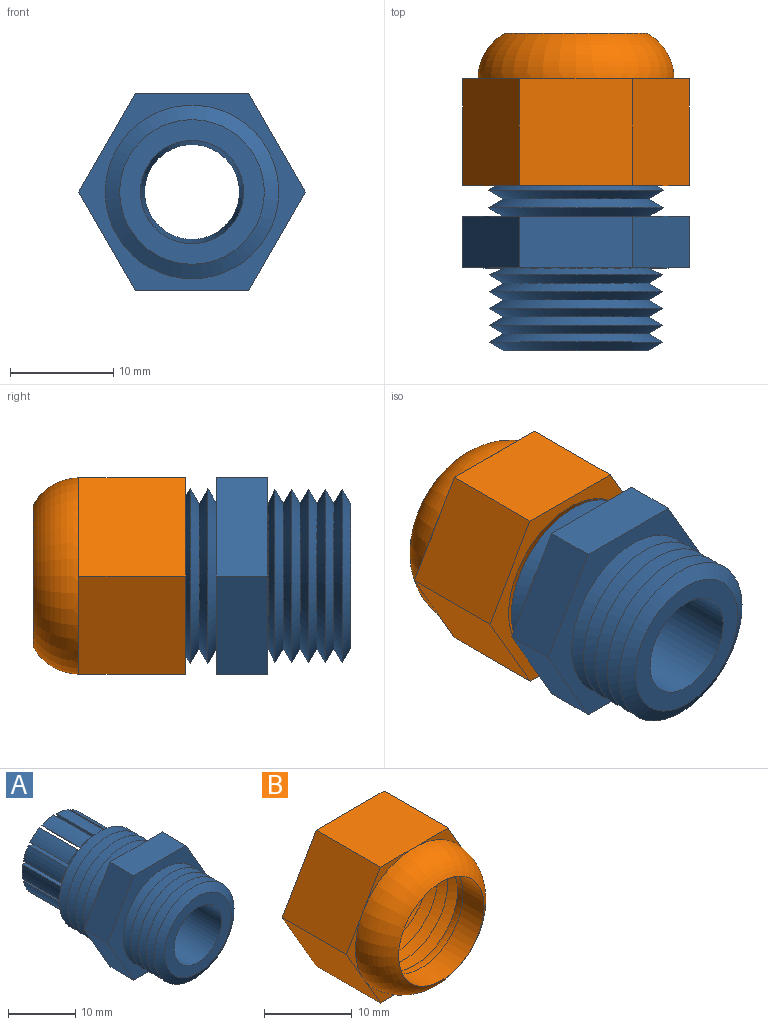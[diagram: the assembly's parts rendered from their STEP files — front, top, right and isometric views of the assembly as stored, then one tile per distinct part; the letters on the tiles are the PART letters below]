
ASSEMBLY  parts=2 mates=1
PART A: 119 faces, bbox 21.9x30x19 mm
  f0: cone r=5.75mm half-angle=2.7deg, axis (0,-1,0), area 15.8mm2, adj f1,f64,f116,f117
  f1: plane 2.55x2.24mm, normal (0,1,0), area 3.7mm2, adj f0,f2,f116,f117
  f2: cylinder r=7mm len=8mm, axis (0,-1,0), area 21mm2, adj f1,f3,f116,f117
  f3: plane 2.55x1mm, normal (0,-1,0), area 1.1mm2, adj f2,f69,f116,f117
  f4: cone r=5.75mm half-angle=2.7deg, axis (0,-1,0), area 15.8mm2, adj f5,f64,f114,f115
  f5: plane 3x1.89mm, normal (0,1,0), area 3.7mm2, adj f4,f6,f114,f115
  f6: cylinder r=7mm len=8mm, axis (0,-1,0), area 21mm2, adj f5,f7,f114,f115
  f7: plane 2.66x0.92mm, normal (0,-1,0), area 1.1mm2, adj f6,f69,f114,f115
  f8: cone r=5.75mm half-angle=2.7deg, axis (0,-1,0), area 15.8mm2, adj f9,f64,f112,f113
  f9: plane 3.16x2.31mm, normal (0,1,0), area 3.7mm2, adj f8,f10,f112,f113
  f10: cylinder r=7mm len=8mm, axis (0,-1,0), area 21mm2, adj f9,f11,f112,f113
  f11: plane 2.33x1.81mm, normal (0,-1,0), area 1.1mm2, adj f10,f69,f112,f113
  f12: cone r=5.75mm half-angle=2.7deg, axis (0,-1,0), area 15.8mm2, adj f13,f64,f110,f111
  f13: plane 2.68x2.36mm, normal (0,1,0), area 3.7mm2, adj f12,f14,f110,f111
  f14: cylinder r=7mm len=8mm, axis (0,-1,0), area 21mm2, adj f13,f15,f110,f111
  f15: plane 2.36x1.53mm, normal (0,-1,0), area 1.1mm2, adj f14,f69,f110,f111
  f16: cone r=5.75mm half-angle=2.7deg, axis (0,-1,0), area 15.8mm2, adj f17,f64,f108,f109
  f17: plane 2.7x1.81mm, normal (0,1,0), area 3.7mm2, adj f16,f18,f108,f109
  f18: cylinder r=7mm len=8mm, axis (0,-1,0), area 21mm2, adj f17,f19,f108,f109
  f19: plane 2.63x0.55mm, normal (0,-1,0), area 1.1mm2, adj f18,f69,f108,f109
  f20: cone r=5.75mm half-angle=2.7deg, axis (0,-1,0), area 15.8mm2, adj f21,f64,f106,f107
  f21: plane 3.16x2.15mm, normal (0,1,0), area 3.7mm2, adj f20,f22,f106,f107
  f22: cylinder r=7mm len=8mm, axis (0,-1,0), area 21mm2, adj f21,f23,f106,f107
  f23: plane 2.56x1.4mm, normal (0,-1,0), area 1.1mm2, adj f22,f69,f106,f107
  f24: cone r=5.75mm half-angle=2.7deg, axis (0,-1,0), area 15.8mm2, adj f25,f64,f104,f105
  f25: plane 3x2.34mm, normal (0,1,0), area 3.7mm2, adj f24,f26,f104,f105
  f26: cylinder r=7mm len=8mm, axis (0,-1,0), area 21mm2, adj f25,f27,f104,f105
  f27: plane 2.12x1.98mm, normal (0,-1,0), area 1.1mm2, adj f26,f69,f104,f105
  f28: cone r=5.75mm half-angle=2.7deg, axis (0,-1,0), area 15.8mm2, adj f29,f64,f102,f103
  f29: plane 2.55x2.24mm, normal (0,1,0), area 3.7mm2, adj f28,f30,f102,f103
  f30: cylinder r=7mm len=8mm, axis (0,-1,0), area 21mm2, adj f29,f31,f102,f103
  f31: plane 2.55x1mm, normal (0,-1,0), area 1.1mm2, adj f30,f69,f102,f103
  f32: cone r=5.75mm half-angle=2.7deg, axis (0,-1,0), area 15.8mm2, adj f33,f64,f100,f101
  f33: plane 3x1.89mm, normal (0,1,0), area 3.7mm2, adj f32,f34,f100,f101
  f34: cylinder r=7mm len=8mm, axis (0,-1,0), area 21mm2, adj f33,f35,f100,f101
  f35: plane 2.66x0.92mm, normal (0,-1,0), area 1.1mm2, adj f34,f69,f100,f101
  f36: cone r=5.75mm half-angle=2.7deg, axis (0,-1,0), area 15.8mm2, adj f37,f64,f98,f99
  f37: plane 3.16x2.31mm, normal (0,1,0), area 3.7mm2, adj f36,f38,f98,f99
  f38: cylinder r=7mm len=8mm, axis (0,-1,0), area 21mm2, adj f37,f39,f98,f99
  f39: plane 2.33x1.81mm, normal (0,-1,0), area 1.1mm2, adj f38,f69,f98,f99
  f40: cone r=5.75mm half-angle=2.7deg, axis (0,-1,0), area 15.8mm2, adj f41,f64,f96,f97
  f41: plane 2.68x2.36mm, normal (0,1,0), area 3.7mm2, adj f40,f42,f96,f97
  f42: cylinder r=7mm len=8mm, axis (0,-1,0), area 21mm2, adj f41,f43,f96,f97
  f43: plane 2.36x1.53mm, normal (0,-1,0), area 1.1mm2, adj f42,f69,f96,f97
  f44: cone r=5.75mm half-angle=2.7deg, axis (0,-1,0), area 15.8mm2, adj f45,f64,f94,f95
  f45: plane 2.7x1.81mm, normal (0,1,0), area 3.7mm2, adj f44,f46,f94,f95
  f46: cylinder r=7mm len=8mm, axis (0,-1,0), area 21mm2, adj f45,f47,f94,f95
  f47: plane 2.63x0.55mm, normal (0,-1,0), area 1.1mm2, adj f46,f69,f94,f95
  f48: cone r=5.75mm half-angle=2.7deg, axis (0,-1,0), area 15.8mm2, adj f49,f64,f92,f93
  f49: plane 3.16x2.15mm, normal (0,1,0), area 3.7mm2, adj f48,f50,f92,f93
  f50: cylinder r=7mm len=8mm, axis (0,-1,0), area 21mm2, adj f49,f51,f92,f93
  f51: plane 2.56x1.4mm, normal (0,-1,0), area 1.1mm2, adj f50,f69,f92,f93
  f52: cone r=8.48mm half-angle=60deg, axis (0,1,0), area 80.3mm2, adj f62,f71
  f53: plane 14x14mm, normal (0,1,0), area 18mm2, adj f54,f69
  f54: cone r=7mm half-angle=60deg, axis (0,-1,0), area 83.2mm2, adj f53,f55
  f55: cone r=8.48mm half-angle=60deg, axis (0,1,0), area 83.2mm2, adj f54,f56
  f56: cone r=7mm half-angle=60deg, axis (0,-1,0), area 83.2mm2, adj f55,f57
  f57: cone r=8.48mm half-angle=60deg, axis (0,1,0), area 83.2mm2, adj f56,f58
  f58: cone r=7mm half-angle=60deg, axis (0,-1,0), area 83.2mm2, adj f57,f59
  f59: cone r=8.48mm half-angle=60deg, axis (0,1,0), area 83.2mm2, adj f58,f60
  f60: cone r=7mm half-angle=60deg, axis (0,-1,0), area 83.2mm2, adj f59,f61
  f61: cone r=8.48mm half-angle=60deg, axis (0,1,0), area 83.2mm2, adj f60,f62
  f62: cone r=7mm half-angle=60deg, axis (0,-1,0), area 83.2mm2, adj f52,f61
  f63: cone r=5mm half-angle=2.7deg, axis (0,-1,0), area 262.5mm2, adj f64,f90
  f64: plane 13.15x12.97mm, normal (0,1,0), area 43.7mm2, adj f0,f4,f8,f12,f16,f20,f24,f28
  f65: cone r=5.75mm half-angle=2.7deg, axis (0,-1,0), area 15.8mm2, adj f64,f66,f91,f118
  f66: plane 3x2.34mm, normal (0,1,0), area 3.7mm2, adj f65,f67,f91,f118
  f67: cylinder r=7mm len=8mm, axis (0,-1,0), area 21mm2, adj f66,f68,f91,f118
  f68: plane 2.12x1.98mm, normal (0,-1,0), area 1.1mm2, adj f67,f69,f91,f118
  f69: cylinder r=6.58mm len=13.15mm, axis (0,-1,0), area 18.4mm2, adj f3,f7,f11,f15,f19,f23,f27,f31
  f70: plane 21.94x19mm, normal (0,-1,0), area 158.7mm2, adj f72,f73,f74,f75,f76,f77,f83
  f71: plane 21.94x19mm, normal (0,1,0), area 156.1mm2, adj f52,f72,f73,f74,f75,f76,f77
  f72: plane 9.5x5.49mm, normal (0.87,0,-0.5), area 54.8mm2, adj f70,f71,f73,f77
  f73: plane 9.5x5.49mm, normal (0.87,0,0.5), area 54.8mm2, adj f70,f71,f72,f74
  f74: plane 10.97x5mm, normal (0,0,1), area 54.8mm2, adj f70,f71,f73,f75
  f75: plane 9.5x5.49mm, normal (-0.87,0,0.5), area 54.8mm2, adj f70,f71,f74,f76
  f76: plane 9.5x5.49mm, normal (-0.87,0,-0.5), area 54.8mm2, adj f70,f71,f75,f77
  f77: plane 10.97x5mm, normal (0,0,-1), area 54.8mm2, adj f70,f71,f72,f76
  f78: cone r=7mm half-angle=60deg, axis (0,-1,0), area 78.8mm2, adj f79,f84
  f79: cone r=8.41mm half-angle=60deg, axis (0,1,0), area 78.8mm2, adj f78,f80
  f80: cone r=7mm half-angle=60deg, axis (0,-1,0), area 78.8mm2, adj f79,f81
  f81: cone r=8.41mm half-angle=60deg, axis (0,1,0), area 78.8mm2, adj f80,f82
  f82: cone r=7mm half-angle=65.6deg, axis (0,-1,0), area 75mm2, adj f81,f83
  f83: cylinder r=7mm len=14mm, axis (0,-1,0), area 1.5mm2, adj f70,f82
  f84: cone r=8.41mm half-angle=60deg, axis (0,1,0), area 78.8mm2, adj f78,f85
  f85: cone r=7mm half-angle=60deg, axis (0,-1,0), area 78.8mm2, adj f84,f86
  f86: cone r=8.41mm half-angle=60deg, axis (0,1,0), area 78.8mm2, adj f85,f87
  f87: cone r=7mm half-angle=60deg, axis (0,-1,0), area 78.8mm2, adj f86,f88
  f88: cone r=8.41mm half-angle=60deg, axis (0,1,0), area 78.8mm2, adj f87,f89
  f89: plane 14x14mm, normal (0,-1,0), area 75.4mm2, adj f88,f90
  f90: cylinder r=5mm len=13.27mm, axis (0,-1,0), area 416.8mm2, adj f63,f89
  f91: plane 8x1.38mm, normal (-0.81,0,0.58), area 11.9mm2, adj f64,f65,f66,f67,f68
  f92: plane 8.01x1.42mm, normal (0.81,0,-0.58), area 12.2mm2, adj f48,f49,f50,f51,f64
  f93: plane 8x1.49mm, normal (-0.48,0,0.88), area 11.9mm2, adj f48,f49,f50,f51,f64
  f94: plane 8.01x1.53mm, normal (0.48,0,-0.88), area 12.2mm2, adj f44,f45,f46,f47,f64
  f95: plane 8x1.69mm, normal (-0.05,0,1), area 11.9mm2, adj f44,f45,f46,f47,f64
  f96: plane 8.01x1.74mm, normal (0.05,0,-1), area 12.2mm2, adj f40,f41,f42,f43,f64
  f97: plane 8x1.56mm, normal (0.39,0,0.92), area 11.9mm2, adj f40,f41,f42,f43,f64
  f98: plane 8.01x1.61mm, normal (-0.39,0,-0.92), area 12.2mm2, adj f36,f37,f38,f39,f64
  f99: plane 8x1.27mm, normal (0.75,0,0.66), area 11.9mm2, adj f36,f37,f38,f39,f64
  f100: plane 8.01x1.31mm, normal (-0.75,0,-0.66), area 12.2mm2, adj f32,f33,f34,f35,f64
  f101: plane 8x1.63mm, normal (0.96,0,0.27), area 11.9mm2, adj f32,f33,f34,f35,f64
  f102: plane 8.01x1.68mm, normal (-0.96,0,-0.27), area 12.2mm2, adj f28,f29,f30,f31,f64
  f103: plane 8x1.67mm, normal (0.99,0,-0.17), area 11.9mm2, adj f28,f29,f30,f31,f64
  f104: plane 8.01x1.72mm, normal (-0.99,0,0.17), area 12.2mm2, adj f24,f25,f26,f27,f64
  f105: plane 8x1.38mm, normal (0.81,0,-0.58), area 11.9mm2, adj f24,f25,f26,f27,f64
  f106: plane 8.01x1.42mm, normal (-0.81,0,0.58), area 12.2mm2, adj f20,f21,f22,f23,f64
  f107: plane 8x1.49mm, normal (0.48,0,-0.88), area 11.9mm2, adj f20,f21,f22,f23,f64
  f108: plane 8.01x1.53mm, normal (-0.48,0,0.88), area 12.2mm2, adj f16,f17,f18,f19,f64
  f109: plane 8x1.69mm, normal (0.05,0,-1), area 11.9mm2, adj f16,f17,f18,f19,f64
  f110: plane 8.01x1.74mm, normal (-0.05,0,1), area 12.2mm2, adj f12,f13,f14,f15,f64
  f111: plane 8x1.56mm, normal (-0.39,0,-0.92), area 11.9mm2, adj f12,f13,f14,f15,f64
  f112: plane 8.01x1.61mm, normal (0.39,0,0.92), area 12.2mm2, adj f8,f9,f10,f11,f64
  f113: plane 8x1.27mm, normal (-0.75,0,-0.66), area 11.9mm2, adj f8,f9,f10,f11,f64
  f114: plane 8.01x1.31mm, normal (0.75,0,0.66), area 12.2mm2, adj f4,f5,f6,f7,f64
  f115: plane 8x1.63mm, normal (-0.96,0,-0.27), area 11.9mm2, adj f4,f5,f6,f7,f64
  f116: plane 8.01x1.68mm, normal (0.96,0,0.27), area 12.2mm2, adj f0,f1,f2,f3,f64
  f117: plane 8x1.67mm, normal (-0.99,0,0.17), area 11.9mm2, adj f0,f1,f2,f3,f64
  f118: plane 8.01x1.72mm, normal (0.99,0,-0.17), area 12.2mm2, adj f64,f65,f66,f67,f68
PART B: 29 faces, bbox 21.9x14.9x19 mm
  f0: plane 8.23x4.75mm, normal (0,-1,0), area 4.9mm2, adj f7,f8,f26
  f1: plane 9.5x2.74mm, normal (0,-1,0), area 4.9mm2, adj f6,f7,f26
  f2: plane 8.23x4.75mm, normal (0,-1,0), area 4.9mm2, adj f6,f11,f26
  f3: plane 8.23x4.75mm, normal (0,-1,0), area 4.9mm2, adj f10,f11,f26
  f4: plane 9.5x2.74mm, normal (0,-1,0), area 4.9mm2, adj f9,f10,f26
  f5: plane 8.23x4.75mm, normal (0,-1,0), area 4.9mm2, adj f8,f9,f26
  f6: plane 10.36x9.5mm, normal (0.87,0,0.5), area 113.6mm2, adj f1,f2,f7,f11,f12
  f7: plane 10.36x9.5mm, normal (0.87,0,-0.5), area 113.6mm2, adj f0,f1,f6,f8,f12
  f8: plane 10.97x10.36mm, normal (0,0,-1), area 113.6mm2, adj f0,f5,f7,f9,f12
  f9: plane 10.36x9.5mm, normal (-0.87,0,-0.5), area 113.6mm2, adj f4,f5,f8,f10,f12
  f10: plane 10.36x9.5mm, normal (-0.87,0,0.5), area 113.6mm2, adj f3,f4,f9,f11,f12
  f11: plane 10.97x10.36mm, normal (0,0,1), area 113.6mm2, adj f2,f3,f6,f10,f12
  f12: plane 21.94x19mm, normal (0,1,0), area 90.4mm2, adj f6,f7,f8,f9,f10,f11,f13
  f13: cone r=8.41mm half-angle=67.3deg, axis (0,1,0), area 74mm2, adj f12,f14
  f14: cone r=7mm half-angle=60deg, axis (0,-1,0), area 78.8mm2, adj f13,f15
  f15: cone r=8.41mm half-angle=60deg, axis (0,1,0), area 78.8mm2, adj f14,f16
  f16: cone r=7mm half-angle=60deg, axis (0,-1,0), area 78.8mm2, adj f15,f17
  f17: cone r=8.41mm half-angle=60deg, axis (0,1,0), area 78.8mm2, adj f16,f18
  f18: cone r=7mm half-angle=60deg, axis (0,-1,0), area 78.8mm2, adj f17,f19
  f19: cone r=8.41mm half-angle=60deg, axis (0,1,0), area 78.8mm2, adj f18,f20
  f20: cone r=7mm half-angle=60deg, axis (0,-1,0), area 78.8mm2, adj f19,f21
  f21: cone r=8.41mm half-angle=60deg, axis (0,1,0), area 78.8mm2, adj f20,f22
  f22: cone r=7mm half-angle=60deg, axis (0,-1,0), area 78.8mm2, adj f21,f23
  f23: cone r=8.41mm half-angle=60deg, axis (0,1,0), area 78.8mm2, adj f22,f24
  f24: cone r=7mm half-angle=60deg, axis (0,-1,0), area 78.8mm2, adj f23,f25
  f25: cone r=8.41mm half-angle=60deg, axis (0,1,0), area 78.8mm2, adj f24,f28
  f26: torus R=4.5mm, axis (0,-1,0), area 289.1mm2, adj f0,f1,f2,f3,f4,f5,f27
  f27: cylinder r=6.9mm len=13.8mm, axis (0,-1,0), area 147mm2, adj f26,f28
  f28: torus R=11.9mm, axis (0,1,0), area 43.6mm2, adj f25,f27
PLACE A t=(5.3,6.57,8.59)mm
PLACE B rot(axis=(1,0,0),180deg) t=(5.3,12.75,8.59)mm
MATE fastened B.f13 <-> A.f0  axis (0,-1,0) through (5.3,7.57,8.59)mm
